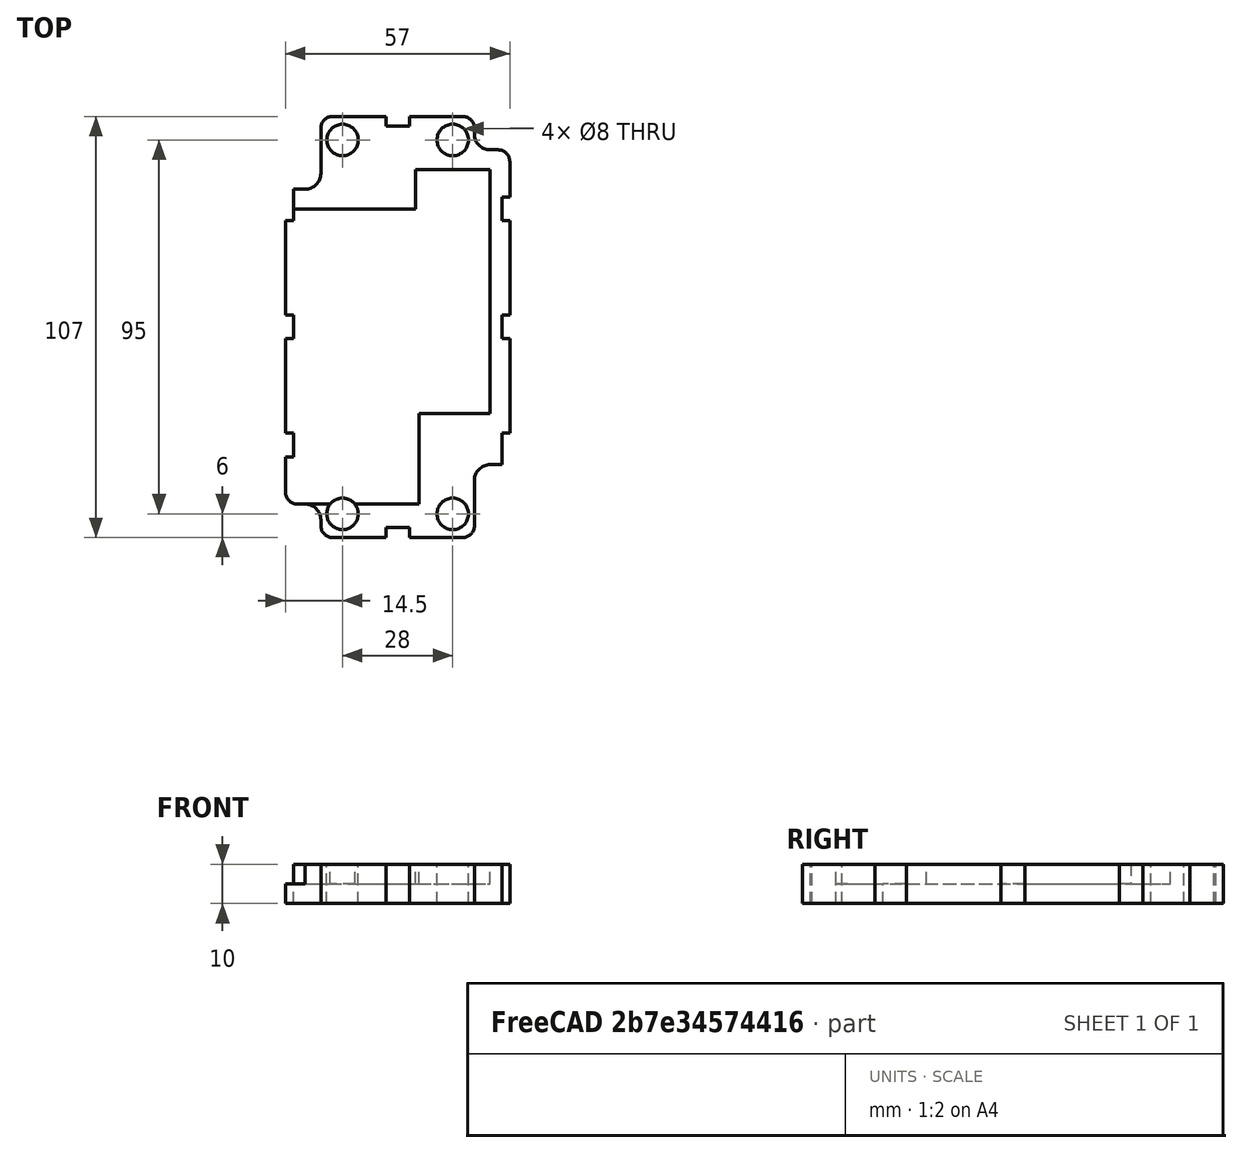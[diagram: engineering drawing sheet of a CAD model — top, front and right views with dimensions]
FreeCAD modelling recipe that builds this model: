
FCSTD DOCUMENT  (FreeCAD 0.16R)
Label: supportSigfox6
License: All rights reserved
LicenseURL: http://en.wikipedia.org/wiki/All_rights_reserved
objects: Part::Box×15, Part::Cylinder×4, Part::MultiFuse×2, Part::Cut×2, PartDesign::Fillet×2
note: 25 computed .brp shape members not serialized (recipe doc carries the construction recipe); baked Part::Feature solids carry a one-line shape summary decoded from their .brp

FEATURE [Part::Box] Box  label="Cube"
  Height = 10
  Length = 57
  Placement = pos=(0,0.5,0) rot=(0,0,1;0rad)
  Width = 107
FEATURE [Part::Box] Box001  label="Cube001"
  Height = 10
  Length = 9
  Placement = pos=(48,0,0) rot=(0,0,1;0rad)
  Width = 19
FEATURE [Part::Box] Box002  label="Cube002"
  Height = 10
  Length = 9
  Width = 9
FEATURE [Part::Box] Box003  label="Cube003"
  Height = 10
  Length = 9
  Placement = pos=(0,89,0) rot=(0,0,1;0rad)
  Width = 19
FEATURE [Part::Box] Box004  label="Cube004"
  Height = 10
  Length = 9
  Placement = pos=(48,99,0) rot=(0,0,1;0rad)
  Width = 9
FEATURE [Part::Box] Box005  label="Cube005"
  Height = 10
  Length = 2
  Placement = pos=(0,51,0) rot=(0,0,1;0rad)
  Width = 6
FEATURE [Part::Box] Box006  label="Cube006"
  Height = 10
  Length = 2
  Placement = pos=(0,81,0) rot=(0,0,1;0rad)
  Width = 8
FEATURE [Part::Box] Box007  label="Cube007"
  Height = 10
  Length = 2
  Placement = pos=(0,21,0) rot=(0,0,1;0rad)
  Width = 6
FEATURE [Part::Box] Box008  label="Cube008"
  Height = 10
  Length = 2
  Placement = pos=(55,51,0) rot=(0,0,1;0rad)
  Width = 6
FEATURE [Part::Box] Box009  label="Cube009"
  Height = 10
  Length = 2
  Placement = pos=(55,81,0) rot=(0,0,1;0rad)
  Width = 6
FEATURE [Part::Box] Box010  label="Cube010"
  Height = 10
  Length = 2
  Placement = pos=(55,19,0) rot=(0,0,1;0rad)
  Width = 8
FEATURE [Part::Cylinder] Cylinder
  Angle = 360
  Height = 10
  Placement = pos=(14.5,6.5,0) rot=(0,0,1;0rad)
  Radius = 4
FEATURE [Part::Cylinder] Cylinder001
  Angle = 360
  Height = 10
  Placement = pos=(42.5,6.5,0) rot=(0,0,1;0rad)
  Radius = 4
FEATURE [Part::Cylinder] Cylinder002
  Angle = 360
  Height = 10
  Placement = pos=(42.5,101.5,0) rot=(0,0,1;0rad)
  Radius = 4
FEATURE [Part::Cylinder] Cylinder003
  Angle = 360
  Height = 10
  Placement = pos=(14.5,101.5,0) rot=(0,0,1;0rad)
  Radius = 4
FEATURE [Part::Box] Box011  label="Cube011"
  Height = 10
  Length = 3
  Placement = pos=(31.5,0,0) rot=(0,0,1;1.5708rad)
  Width = 6
FEATURE [Part::Box] Box012  label="Cube012"
  Height = 10
  Length = 3
  Placement = pos=(31.5,105,0) rot=(0,0,1;1.5708rad)
  Width = 6
FEATURE [Part::MultiFuse] Fusion
  Shapes = -> [Box001,Box002,Box003,Box004,Box005,Box006,Box007,Box008,Box009,Box010,Cylinder,Cylinder002,Cylinder001,Cylinder003,Box011,Box012]
FEATURE [Part::Cut] Cut
  Base = -> Box
  Tool = -> Fusion
FEATURE [PartDesign::Fillet] Fillet
  Base = -> Cut [Edge103,Edge108,Edge110,Edge123,Edge128,Edge4]
  Radius = 3
FEATURE [PartDesign::Fillet] Fillet001
  Base = -> Fillet [Edge124,Edge142,Edge105,Edge123]
  Radius = 4
FEATURE [Part::Box] Box014  label="Cube014"
  Height = 10
  Length = 19
  Placement = pos=(33,32,5) rot=(0,0,1;0rad)
  Width = 62
FEATURE [Part::Box] Box013  label="Cube013"
  Height = 10
  Length = 34
  Placement = pos=(0,9,5) rot=(0,0,1;0rad)
  Width = 75
FEATURE [Part::MultiFuse] Fusion001
  Shapes = -> [Box013,Box014]
FEATURE [Part::Cut] Cut001
  Base = -> Fillet001
  Tool = -> Fusion001
